# Revit family: Arper_Aava-02_trestle-swivel_wood_7626
name_source: partatom
category: Furniture
units: mm (PartAtom-declared; Revit-internal decimal feet)

## family parameters
Always vertical = Yes
Cut with Voids When Loaded = No
OmniClass Number = 23.40.20.00
OmniClass Title = General Furniture and Specialties
Room Calculation Point = No
Shared = No
Work Plane-Based = No

## types (1)
- Arper_Aava-02_trestle-swivel_wood_7626
    Default Elevation = 0 mm  [stored 0 ft]
    Description = Chair with polished or powdercoated aluminium swivel trestle base
and reconstituted veneer shell, natural or stained birchwood effect in
4 different colours. Optional glides with felt for wooden floors are
available upon request. A non-washable, removable cover (Item
3920) is also available in leather, faux leather, fabric or customer's
material allowing the chair to be used in two versions: wood or
upholstered.
    Manufacturer = ARPER s.p.a.
    Model = Aava 02
    URL = http://www.arper.com

note: [stored X ft] marks values corroborated as IEEE doubles in the binary element streams (Revit-internal decimal feet)
